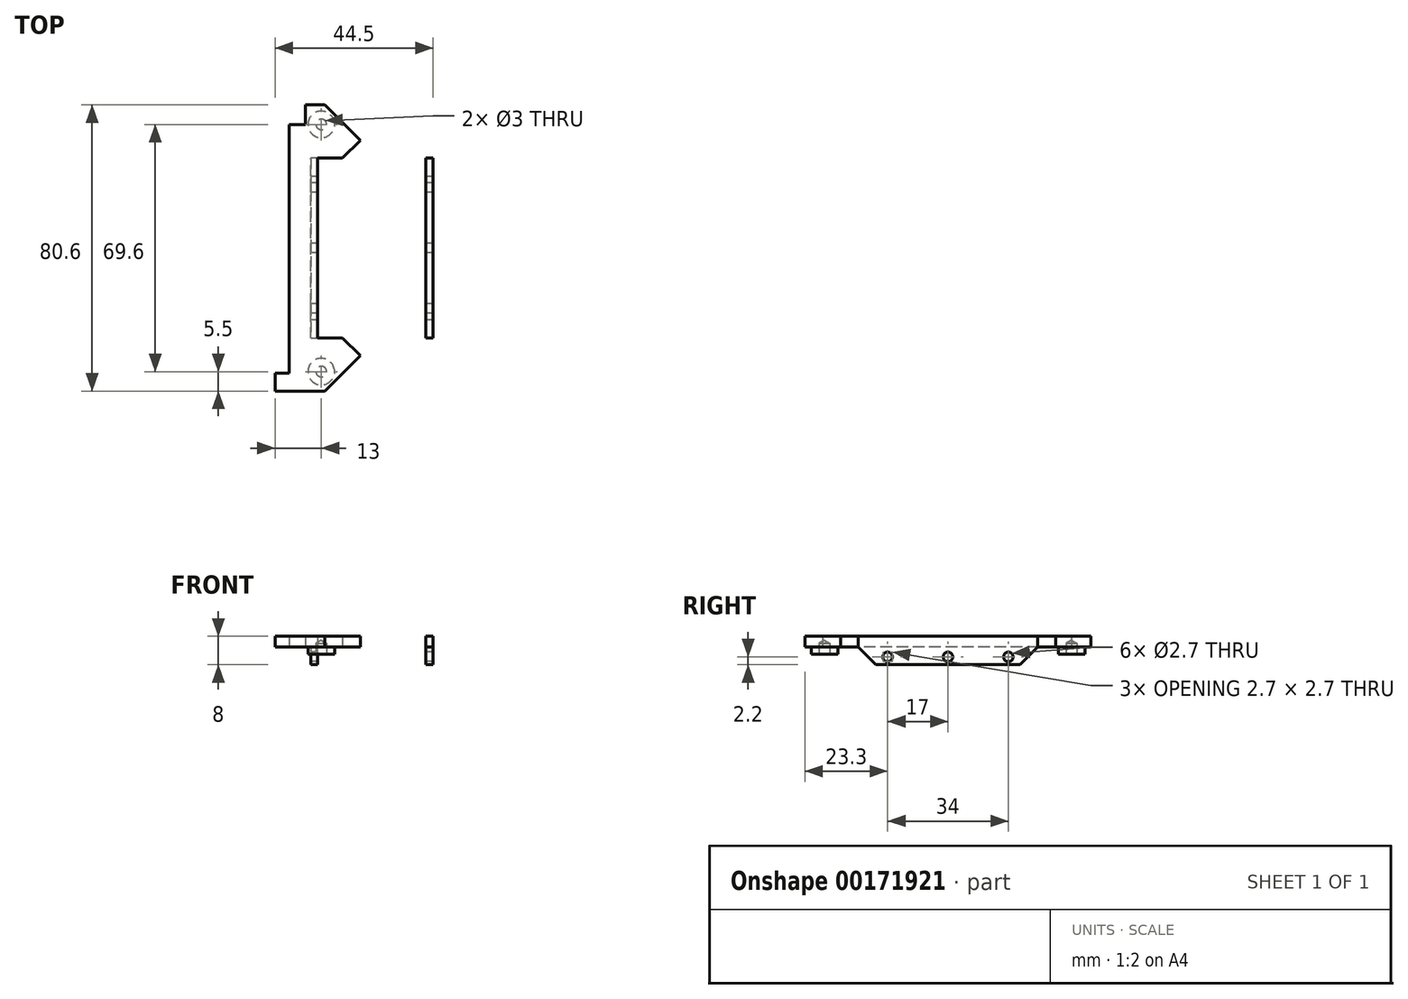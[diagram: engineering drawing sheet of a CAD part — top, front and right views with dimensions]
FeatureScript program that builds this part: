
annotation { "Feature Type Name" : "Feature", "Feature Type Description" : "" }
export const myFeature = defineFeature(function(context is Context, id is Id, definition is map)
    precondition{}
    {
        {
            var Q0;
            Q0=qCreatedBy(makeId("Top.planeOp"),FACE);
            var sketch = newSketch(context, id + "F0", { "sketchPlane" : qUnion([Q0])});
            skLineSegment(sketch, "E0.bottom", {"start": v(18.25, -12.65) * mm, "end": v(-18.25, -12.65) * mm});
            skLineSegment(sketch, "E0.top", {"start": v(18.25, 12.65) * mm, "end": v(-18.25, 12.65) * mm});
            skLineSegment(sketch, "E0.left", {"start": v(18.25, -12.65) * mm, "end": v(18.25, 12.65) * mm});
            skLineSegment(sketch, "E0.right", {"start": v(-18.25, -12.65) * mm, "end": v(-18.25, 12.65) * mm});
            skPoint(sketch, "E0.middle", {"position": v(0, 0) * mm});
            skLineSegment(sketch, "E1.bottom", {"start": v(-15.25, 12.65) * mm, "end": v(15.25, 12.65) * mm});
            skLineSegment(sketch, "E1.top", {"start": v(-15.25, -12.65) * mm, "end": v(15.25, -12.65) * mm});
            skLineSegment(sketch, "E1.left", {"start": v(-15.25, 12.65) * mm, "end": v(-15.25, -12.65) * mm});
            skLineSegment(sketch, "E1.right", {"start": v(15.25, 12.65) * mm, "end": v(15.25, -12.65) * mm});
            skSolve(sketch);
        }
        {
            var Q0;
            {var subQ0=sQuery(id+"F0.wireOp",EDGE,"E0.left");Q0=makeQuery(id+"F0.imprint","IMPRINT",FACE,{"disambiguationData":[TD([[makeQuery(id+"F0.imprint","IMPRINT",EDGE,{"derivedFrom":subQ0}),1.0]])]});}
            var Q1;
            Q1=makeQuery(id+"F0.imprint","IMPRINT",FACE,{"disambiguationData":[TD([[makeQuery(id+"F0.imprint","IMPRINT",EDGE,{"derivedFrom":sQuery(id+"F0.wireOp",EDGE,"E1.bottom")}),-1.0]])]});
            var Q2;
            {var subQ0=sQuery(id+"F0.wireOp",EDGE,"E0.right");Q2=makeQuery(id+"F0.imprint","IMPRINT",FACE,{"disambiguationData":[TD([[makeQuery(id+"F0.imprint","IMPRINT",EDGE,{"derivedFrom":subQ0}),-1.0]])]});}
            extrude(context, id + "F1", {"entities" : qUnion([Q0, Q1, Q2]), "depth" : 3 * mm});
        }
        {
            var Q0;
            {var subQ0=sQuery(id+"F0.wireOp",EDGE,"E0.left");Q0=makeQuery(id+"F0.imprint","IMPRINT",FACE,{"disambiguationData":[TD([[makeQuery(id+"F0.imprint","IMPRINT",EDGE,{"derivedFrom":subQ0}),1.0]])]});}
            var Q1;
            {var subQ0=sQuery(id+"F0.wireOp",EDGE,"E0.right");Q1=makeQuery(id+"F0.imprint","IMPRINT",FACE,{"disambiguationData":[TD([[makeQuery(id+"F0.imprint","IMPRINT",EDGE,{"derivedFrom":subQ0}),-1.0]])]});}
            extrude(context, id + "F2", {"entities" : qUnion([Q0, Q1]), "operationType" : NewBodyOperationType.ADD, "oppositeDirection" : true, "depth" : 5 * mm});
        }
        {
            var Q0;
            Q0=makeQuery(id+"F2.opExtrude","SWEPT_FACE",FACE,{"disambiguationData":[OSD([sQuery(id+"F0.wireOp",EDGE,"E1.right")])]});
            var sketch = newSketch(context, id + "F3", { "sketchPlane" : qUnion([Q0])});
            skLineSegment(sketch, "E2", {"start": v(0, -2.9) * mm, "end": v(0, 13.46) * mm, "construction": true});
            skLineSegment(sketch, "E3", {"start": v(-11.7, -5) * mm, "end": v(7.83, -5) * mm, "construction": true});
            skLineSegment(sketch, "E4", {"start": v(18.8, 0) * mm, "end": v(-9.4, 0) * mm, "construction": true});
            skCircle(sketch, "E5", {"center": v(12.65, -2.8) * mm, "radius": 1.35 * mm});
            skCircle(sketch, "E6", {"center": v(-4.35, -2.8) * mm, "radius": 1.35 * mm});
            skCircle(sketch, "E7.0", {"center": v(-4.35, -2.8) * mm, "radius": 2.35 * mm});
            skCircle(sketch, "E8.0", {"center": v(12.65, -2.8) * mm, "radius": 2.35 * mm});
            skSolve(sketch);
        }
        {
            var Q0;
            {var subQ0=sQuery(id+"F3.wireOp",EDGE,"E5");var subQ1=makeQuery(id+"F2.opExtrude","SWEPT_EDGE",EDGE,{"disambiguationData":[OSD([sQuery(id+"F0.wireOp",EDGE,"E0.bottom"),sQuery(id+"F0.wireOp",EDGE,"E1.top"),sQuery(id+"F0.wireOp",EDGE,"E1.right")])]});var subQ2=makeQuery(id+"F3.imprint","INTERSECT",VERTEX,{"disambiguationData":[OD(0.0)],"derivedFrom":[subQ1,subQ0]});Q0=makeQuery(id+"F3.imprint","IMPRINT",FACE,{"disambiguationData":[TD([[makeQuery(id+"F3.imprint","IMPRINT",EDGE,{"disambiguationData":[TD([[subQ2,1.0]])],"derivedFrom":subQ0}),1.0]])]});}
            var Q1;
            Q1=makeQuery(id+"F3.imprint","IMPRINT",FACE,{"disambiguationData":[TD([[makeQuery(id+"F3.imprint","IMPRINT",EDGE,{"derivedFrom":sQuery(id+"F3.wireOp",EDGE,"E6")}),1.0]])]});
            extrude(context, id + "F4", {"entities" : qUnion([Q0, Q1]), "operationType" : NewBodyOperationType.REMOVE, "endBound" : BoundingType.SYMMETRIC, "oppositeDirection" : true, "depth" : 1000 * mm});
        }
        {
            var Q0;
            Q0=qCreatedBy(makeId("Front.planeOp"),FACE);
            cPlane(context, id + "F5", {"entities" : qUnion([Q0]), "cplaneType" : CPlaneType.OFFSET, "offset" : 12.65 * mm, "width" : 150 * mm, "height" : 150 * mm});
        }
        {
            var Q0;
            Q0=makeQuery(id+"F1.opExtrude","SWEPT_BODY",BODY,{"disambiguationData":[OSD([sQuery(id+"F0.wireOp",EDGE,"E0.left"),sQuery(id+"F0.wireOp",EDGE,"E0.right"),sQuery(id+"F0.wireOp",EDGE,"E1.bottom"),sQuery(id+"F0.wireOp",EDGE,"E1.top")])]});
            var Q1;
            Q1=qCreatedBy(id+"F5.planeOp",FACE);
            mirror(context, id + "F6", {"operationType" : NewBodyOperationType.ADD, "entities" : qUnion([Q0]), "mirrorPlane" : qUnion([Q1])});
        }
        {
            var Q0;
            {var subQ0=sQuery(id+"F0.wireOp",EDGE,"E0.top");Q0=makeQuery(id+"F2.opExtrude","CAP_EDGE",EDGE,{"disambiguationData":[OSD([subQ0]),TDD([makeQuery(id+"F0.imprint","IMPRINT",EDGE,{"disambiguationData":[TD([[makeQuery(id+"F0.imprint","INTERSECT",VERTEX,{"derivedFrom":[subQ0,sQuery(id+"F0.wireOp",EDGE,"E0.right")]}),1.0]])],"derivedFrom":subQ0})])],"isStart":false});}
            var Q1;
            {var subQ0=sQuery(id+"F0.wireOp",EDGE,"E0.top");Q1=makeQuery(id+"F2.opExtrude","CAP_EDGE",EDGE,{"disambiguationData":[OSD([subQ0]),TDD([makeQuery(id+"F0.imprint","IMPRINT",EDGE,{"disambiguationData":[TD([[makeQuery(id+"F0.imprint","INTERSECT",VERTEX,{"derivedFrom":[subQ0,sQuery(id+"F0.wireOp",EDGE,"E0.left")]}),-1.0]])],"derivedFrom":subQ0})])],"isStart":false});}
            var Q2;
            {var subQ0=sQuery(id+"F0.wireOp",EDGE,"E0.top");Q2=makeQuery(id+"F6.opPattern","COPY",EDGE,{"derivedFrom":makeQuery(id+"F2.opExtrude","CAP_EDGE",EDGE,{"disambiguationData":[OSD([subQ0]),TDD([makeQuery(id+"F0.imprint","IMPRINT",EDGE,{"disambiguationData":[TD([[makeQuery(id+"F0.imprint","INTERSECT",VERTEX,{"derivedFrom":[subQ0,sQuery(id+"F0.wireOp",EDGE,"E0.left")]}),-1.0]])],"derivedFrom":subQ0})])],"isStart":false}),"instanceName":"1"});}
            var Q3;
            {var subQ0=sQuery(id+"F0.wireOp",EDGE,"E0.top");Q3=makeQuery(id+"F6.opPattern","COPY",EDGE,{"derivedFrom":makeQuery(id+"F2.opExtrude","CAP_EDGE",EDGE,{"disambiguationData":[OSD([subQ0]),TDD([makeQuery(id+"F0.imprint","IMPRINT",EDGE,{"disambiguationData":[TD([[makeQuery(id+"F0.imprint","INTERSECT",VERTEX,{"derivedFrom":[subQ0,sQuery(id+"F0.wireOp",EDGE,"E0.right")]}),1.0]])],"derivedFrom":subQ0})])],"isStart":false}),"instanceName":"1"});}
            chamfer(context, id + "F7", {"entities" : qUnion([Q0, Q1, Q2, Q3]), "width" : 5 * mm, "tangentPropagation" : true});
        }
        {
            var Q0;
            {var subQ0=sQuery(id+"F0.wireOp",EDGE,"E0.right");var subQ1=makeQuery(id+"F2.boolean.opBoolean","MERGE",FACE,{"derivedFrom":[makeQuery(id+"F1.opExtrude","SWEPT_FACE",FACE,{"disambiguationData":[OSD([subQ0])]}),makeQuery(id+"F2.opExtrude","SWEPT_FACE",FACE,{"disambiguationData":[OSD([subQ0])]})]});Q0=makeQuery(id+"F6.boolean.opBoolean","MERGE",FACE,{"derivedFrom":[subQ1,makeQuery(id+"F6.opPattern","COPY",FACE,{"derivedFrom":subQ1,"instanceName":"1"})]});}
            var sketch = newSketch(context, id + "F8", { "sketchPlane" : qUnion([Q0])});
            skLineSegment(sketch, "E9.bottom", {"start": v(-12.65, 0) * mm, "end": v(37.95, 0) * mm});
            skLineSegment(sketch, "E9.top", {"start": v(-12.65, -6.32) * mm, "end": v(37.95, -6.32) * mm});
            skLineSegment(sketch, "E9.left", {"start": v(-12.65, 0) * mm, "end": v(-12.65, -6.32) * mm});
            skLineSegment(sketch, "E9.right", {"start": v(37.95, 0) * mm, "end": v(37.95, -6.32) * mm});
            skSolve(sketch);
        }
        {
            var Q0;
            Q0=makeQuery(id+"F8.imprint","IMPRINT",FACE,{"disambiguationData":[TD([[makeQuery(id+"F8.imprint","IMPRINT",EDGE,{"derivedFrom":sQuery(id+"F8.wireOp",EDGE,"E9.bottom")}),-1.0]])]});
            extrude(context, id + "F9", {"entities" : qUnion([Q0]), "operationType" : NewBodyOperationType.REMOVE, "oppositeDirection" : true, "depth" : 1 * mm});
        }
        {
            var Q0;
            Q0=qCreatedBy(makeId("Top.planeOp"),FACE);
            var sketch = newSketch(context, id + "F10", { "sketchPlane" : qUnion([Q0])});
            skLineSegment(sketch, "E10.bottom", {"start": v(-18.25, -37.95) * mm, "end": v(-3.25, -37.95) * mm});
            skLineSegment(sketch, "E10.top", {"start": v(-18.25, -52.95) * mm, "end": v(-3.25, -52.95) * mm});
            skLineSegment(sketch, "E10.left", {"start": v(-18.25, -37.95) * mm, "end": v(-18.25, -52.95) * mm});
            skLineSegment(sketch, "E10.right", {"start": v(-3.25, -37.95) * mm, "end": v(-3.25, -52.95) * mm});
            skLineSegment(sketch, "E11.bottom", {"start": v(-18.25, 12.65) * mm, "end": v(-3.25, 12.65) * mm});
            skLineSegment(sketch, "E11.top", {"start": v(-18.25, 27.65) * mm, "end": v(-3.25, 27.65) * mm});
            skLineSegment(sketch, "E11.left", {"start": v(-18.25, 12.65) * mm, "end": v(-18.25, 27.65) * mm});
            skLineSegment(sketch, "E11.right", {"start": v(-3.25, 12.65) * mm, "end": v(-3.25, 27.65) * mm});
            skSolve(sketch);
        }
        {
            var Q0;
            Q0 = qSketchRegion(id + "F10", true);
            extrude(context, id + "F11", {"entities" : qUnion([Q0]), "operationType" : NewBodyOperationType.ADD, "depth" : 3 * mm});
        }
        {
            var Q0;
            {var subQ0=makeQuery(id+"F1.opExtrude","CAP_FACE",FACE,{"disambiguationData":[OSD([sQuery(id+"F0.wireOp",EDGE,"E0.bottom"),sQuery(id+"F0.wireOp",EDGE,"E0.top"),sQuery(id+"F0.wireOp",EDGE,"E0.left"),sQuery(id+"F0.wireOp",EDGE,"E0.right"),sQuery(id+"F0.wireOp",EDGE,"E1.bottom"),sQuery(id+"F0.wireOp",EDGE,"E1.top")])],"isStart":true});Q0=makeQuery(id+"F11.boolean.opBoolean","MERGE",FACE,{"derivedFrom":[makeQuery(id+"F6.boolean.opBoolean","MERGE",FACE,{"derivedFrom":[subQ0,makeQuery(id+"F6.opPattern","COPY",FACE,{"derivedFrom":subQ0,"instanceName":"1"})]}),makeQuery(id+"F9.boolean.opBoolean","COPY",FACE,{"derivedFrom":makeQuery(id+"F9.opExtrude","SWEPT_FACE",FACE,{"disambiguationData":[OSD([sQuery(id+"F8.wireOp",EDGE,"E9.bottom")])]})}),makeQuery(id+"F11.opExtrude","CAP_FACE",FACE,{"disambiguationData":[OSD([sQuery(id+"F10.wireOp",EDGE,"pW5Quktj-L34n-hhZY-v1Ix-rfs9Iihu1468.bottom"),sQuery(id+"F10.wireOp",EDGE,"pW5Quktj-L34n-hhZY-v1Ix-rfs9Iihu1468.top"),sQuery(id+"F10.wireOp",EDGE,"pW5Quktj-L34n-hhZY-v1Ix-rfs9Iihu1468.left"),sQuery(id+"F10.wireOp",EDGE,"pW5Quktj-L34n-hhZY-v1Ix-rfs9Iihu1468.right")])],"isStart":true}),makeQuery(id+"F11.opExtrude","CAP_FACE",FACE,{"disambiguationData":[OSD([sQuery(id+"F10.wireOp",EDGE,"H2ijIvu5-2ODO-Xeke-0aQG-66x5qS3q1Ywc.bottom"),sQuery(id+"F10.wireOp",EDGE,"H2ijIvu5-2ODO-Xeke-0aQG-66x5qS3q1Ywc.top"),sQuery(id+"F10.wireOp",EDGE,"H2ijIvu5-2ODO-Xeke-0aQG-66x5qS3q1Ywc.left"),sQuery(id+"F10.wireOp",EDGE,"H2ijIvu5-2ODO-Xeke-0aQG-66x5qS3q1Ywc.right")])],"isStart":true})]});}
            var sketch = newSketch(context, id + "F12", { "sketchPlane" : qUnion([Q0])});
            skLineSegment(sketch, "E12.bottom", {"start": v(-18.25, 52.95) * mm, "end": v(-22.25, 52.95) * mm});
            skLineSegment(sketch, "E12.top", {"start": v(-18.25, 47.95) * mm, "end": v(-22.25, 47.95) * mm});
            skLineSegment(sketch, "E12.left", {"start": v(-18.25, 52.95) * mm, "end": v(-18.25, 47.95) * mm});
            skLineSegment(sketch, "E12.right", {"start": v(-22.25, 52.95) * mm, "end": v(-22.25, 47.95) * mm});
            skLineSegment(sketch, "E13.bottom", {"start": v(-18.25, -27.65) * mm, "end": v(-13.75, -27.65) * mm});
            skLineSegment(sketch, "E13.top", {"start": v(-18.25, -22.15) * mm, "end": v(-13.75, -22.15) * mm});
            skLineSegment(sketch, "E13.left", {"start": v(-18.25, -27.65) * mm, "end": v(-18.25, -22.15) * mm});
            skLineSegment(sketch, "E13.right", {"start": v(-13.75, -27.65) * mm, "end": v(-13.75, -22.15) * mm});
            skSolve(sketch);
        }
        {
            var Q0;
            Q0=makeQuery(id+"F12.imprint","IMPRINT",FACE,{"disambiguationData":[TD([[makeQuery(id+"F12.imprint","IMPRINT",EDGE,{"derivedFrom":sQuery(id+"F12.wireOp",EDGE,"E12.bottom")}),1.0]])]});
            extrude(context, id + "F13", {"entities" : qUnion([Q0]), "operationType" : NewBodyOperationType.ADD, "oppositeDirection" : true, "depth" : 3 * mm});
        }
        {
            var Q0;
            Q0=makeQuery(id+"F12.imprint","IMPRINT",FACE,{"disambiguationData":[TD([[makeQuery(id+"F12.imprint","IMPRINT",EDGE,{"derivedFrom":sQuery(id+"F12.wireOp",EDGE,"E13.bottom")}),1.0]])]});
            extrude(context, id + "F14", {"entities" : qUnion([Q0]), "operationType" : NewBodyOperationType.REMOVE, "oppositeDirection" : true, "depth" : 25 * mm});
        }
        {
            var Q0;
            {var subQ0=sQuery(id+"F0.wireOp",EDGE,"E0.right");var subQ1=makeQuery(id+"F2.boolean.opBoolean","MERGE",FACE,{"derivedFrom":[makeQuery(id+"F1.opExtrude","SWEPT_FACE",FACE,{"disambiguationData":[OSD([subQ0])]}),makeQuery(id+"F2.opExtrude","SWEPT_FACE",FACE,{"disambiguationData":[OSD([subQ0])]})]});Q0=makeQuery(id+"F11.boolean.opBoolean","MERGE",FACE,{"derivedFrom":[makeQuery(id+"F6.boolean.opBoolean","MERGE",FACE,{"derivedFrom":[subQ1,makeQuery(id+"F6.opPattern","COPY",FACE,{"derivedFrom":subQ1,"instanceName":"1"})]}),makeQuery(id+"F11.opExtrude","SWEPT_FACE",FACE,{"disambiguationData":[OSD([sQuery(id+"F10.wireOp",EDGE,"E10.left")])]}),makeQuery(id+"F11.opExtrude","SWEPT_FACE",FACE,{"disambiguationData":[OSD([sQuery(id+"F10.wireOp",EDGE,"E11.left")])]})]});}
            var Q1;
            Q1=makeQuery(id+"F13.opExtrude","SWEPT_FACE",FACE,{"disambiguationData":[OSD([sQuery(id+"F12.wireOp",EDGE,"E12.right")])]});
            var Q2;
            Q2=makeQuery(id+"F14.boolean.opBoolean","COPY",FACE,{"derivedFrom":makeQuery(id+"F14.opExtrude","SWEPT_FACE",FACE,{"disambiguationData":[OSD([sQuery(id+"F12.wireOp",EDGE,"E13.right")])]})});
            extrude(context, id + "F15", {"entities" : qUnion([Q0, Q1, Q2]), "operationType" : NewBodyOperationType.ADD, "depth" : 5 * mm});
        }
        {
            var Q0;
            {var subQ0=sQuery(id+"F10.wireOp",EDGE,"E11.left");var subQ1=sQuery(id+"F10.wireOp",EDGE,"E10.left");var subQ2=sQuery(id+"F8.wireOp",EDGE,"E9.bottom");var subQ3=sQuery(id+"F12.wireOp",EDGE,"E12.right");var subQ4=makeQuery(id+"F1.opExtrude","CAP_FACE",FACE,{"disambiguationData":[OSD([sQuery(id+"F0.wireOp",EDGE,"E0.bottom"),sQuery(id+"F0.wireOp",EDGE,"E0.top"),sQuery(id+"F0.wireOp",EDGE,"E0.left"),sQuery(id+"F0.wireOp",EDGE,"E0.right"),sQuery(id+"F0.wireOp",EDGE,"E1.bottom"),sQuery(id+"F0.wireOp",EDGE,"E1.top")])],"isStart":true});Q0=makeQuery(id+"F15.boolean.opBoolean","MERGE",FACE,{"derivedFrom":[makeQuery(id+"F13.boolean.opBoolean","MERGE",FACE,{"derivedFrom":[makeQuery(id+"F11.boolean.opBoolean","MERGE",FACE,{"derivedFrom":[makeQuery(id+"F6.boolean.opBoolean","MERGE",FACE,{"derivedFrom":[subQ4,makeQuery(id+"F6.opPattern","COPY",FACE,{"derivedFrom":subQ4,"instanceName":"1"})]}),makeQuery(id+"F9.boolean.opBoolean","COPY",FACE,{"derivedFrom":makeQuery(id+"F9.opExtrude","SWEPT_FACE",FACE,{"disambiguationData":[OSD([subQ2])]})}),makeQuery(id+"F11.opExtrude","CAP_FACE",FACE,{"disambiguationData":[OSD([sQuery(id+"F10.wireOp",EDGE,"E10.bottom"),sQuery(id+"F10.wireOp",EDGE,"E10.top"),subQ1,sQuery(id+"F10.wireOp",EDGE,"E10.right")])],"isStart":true}),makeQuery(id+"F11.opExtrude","CAP_FACE",FACE,{"disambiguationData":[OSD([sQuery(id+"F10.wireOp",EDGE,"E11.bottom"),sQuery(id+"F10.wireOp",EDGE,"E11.top"),subQ0,sQuery(id+"F10.wireOp",EDGE,"E11.right")])],"isStart":true})]}),makeQuery(id+"F13.opExtrude","CAP_FACE",FACE,{"disambiguationData":[OSD([sQuery(id+"F12.wireOp",EDGE,"E12.bottom"),sQuery(id+"F12.wireOp",EDGE,"E12.top"),sQuery(id+"F12.wireOp",EDGE,"E12.left"),subQ3])],"isStart":true})]}),makeQuery(id+"F15.opExtrude","SWEPT_FACE",FACE,{"disambiguationData":[OSD([subQ3]),TDD([makeQuery(id+"F13.opExtrude","CAP_EDGE",EDGE,{"disambiguationData":[OSD([subQ3])],"isStart":true})])]}),makeQuery(id+"F15.opExtrude","SWEPT_FACE",FACE,{"disambiguationData":[OSD([sQuery(id+"F12.wireOp",EDGE,"E13.right")])]}),makeQuery(id+"F15.opExtrude","SWEPT_FACE",FACE,{"disambiguationData":[OSD([subQ2,subQ1,subQ0])]})]});}
            var sketch = newSketch(context, id + "F16", { "sketchPlane" : qUnion([Q0])});
            skCircle(sketch, "E14", {"center": v(-14.25, 47.45) * mm, "radius": 3.75 * mm});
            skCircle(sketch, "E15", {"center": v(-14.25, -22.15) * mm, "radius": 3.75 * mm});
            skSolve(sketch);
        }
        {
            var Q0;
            Q0=makeQuery(id+"F16.imprint","IMPRINT",FACE,{"disambiguationData":[TD([[makeQuery(id+"F16.imprint","IMPRINT",EDGE,{"derivedFrom":sQuery(id+"F16.wireOp",EDGE,"E15")}),1.0]])]});
            var Q1;
            Q1=makeQuery(id+"F16.imprint","IMPRINT",FACE,{"disambiguationData":[TD([[makeQuery(id+"F16.imprint","IMPRINT",EDGE,{"derivedFrom":sQuery(id+"F16.wireOp",EDGE,"E14")}),1.0]])]});
            extrude(context, id + "F17", {"entities" : qUnion([Q0, Q1]), "operationType" : NewBodyOperationType.ADD, "depth" : 2 * mm});
        }
        {
            var Q0;
            Q0=makeQuery(id+"F17.opExtrude","CAP_FACE",FACE,{"disambiguationData":[OSD([sQuery(id+"F16.wireOp",EDGE,"E14")])],"isStart":false});
            var sketch = newSketch(context, id + "F18", { "sketchPlane" : qUnion([Q0])});
            skCircle(sketch, "E16", {"center": v(-14.25, 47.45) * mm, "radius": 1 * mm});
            skSolve(sketch);
        }
        {
            var Q0;
            Q0=makeQuery(id+"F17.opExtrude","CAP_FACE",FACE,{"disambiguationData":[OSD([sQuery(id+"F16.wireOp",EDGE,"E15")])],"isStart":false});
            var sketch = newSketch(context, id + "F19", { "sketchPlane" : qUnion([Q0])});
            skCircle(sketch, "E17", {"center": v(-14.25, -22.15) * mm, "radius": 1 * mm});
            skSolve(sketch);
        }
        {
            var Q0;
            Q0=sQuery(id+"F18.wireOp",VERTEX,"E16.center");
            var Q1;
            Q1=sQuery(id+"F19.wireOp",VERTEX,"E17.center");
            var Q2;
            Q2=makeQuery(id+"F1.opExtrude","SWEPT_BODY",BODY,{"disambiguationData":[OSD([sQuery(id+"F0.wireOp",EDGE,"E0.bottom"),sQuery(id+"F0.wireOp",EDGE,"E0.top"),sQuery(id+"F0.wireOp",EDGE,"E0.left"),sQuery(id+"F0.wireOp",EDGE,"E0.right"),sQuery(id+"F0.wireOp",EDGE,"E1.bottom"),sQuery(id+"F0.wireOp",EDGE,"E1.top")])]});
            hole(context, id + "F20", {"style" : HoleStyle.C_BORE, "endStyle" : HoleEndStyle.BLIND, "holeDiameter" : 3 * mm, "cBoreDiameter" : 3 * mm, "cBoreDepth" : 3 * mm, "holeDepth" : 3 * mm, "tappedDepth" : 12 * mm, "tapClearance" : 3, "locations" : qUnion([Q0, Q1]), "scope" : qUnion([Q2])});
        }
        {
            var Q0;
            Q0=makeQuery(id+"F11.opExtrude","SWEPT_EDGE",EDGE,{"disambiguationData":[OSD([sQuery(id+"F10.wireOp",EDGE,"E11.top"),sQuery(id+"F10.wireOp",EDGE,"E11.right")])]});
            var Q1;
            Q1=makeQuery(id+"F11.opExtrude","SWEPT_EDGE",EDGE,{"disambiguationData":[OSD([sQuery(id+"F10.wireOp",EDGE,"E10.top"),sQuery(id+"F10.wireOp",EDGE,"E10.right")])]});
            chamfer(context, id + "F21", {"entities" : qUnion([Q0, Q1]), "width" : 10 * mm, "tangentPropagation" : true});
        }
        {
            var Q0;
            {var subQ0=sQuery(id+"F0.wireOp",EDGE,"E0.left");var subQ1=makeQuery(id+"F2.boolean.opBoolean","MERGE",FACE,{"derivedFrom":[makeQuery(id+"F1.opExtrude","SWEPT_FACE",FACE,{"disambiguationData":[OSD([subQ0])]}),makeQuery(id+"F2.opExtrude","SWEPT_FACE",FACE,{"disambiguationData":[OSD([subQ0])]})]});Q0=makeQuery(id+"F6.boolean.opBoolean","MERGE",FACE,{"derivedFrom":[subQ1,makeQuery(id+"F6.opPattern","COPY",FACE,{"derivedFrom":subQ1,"instanceName":"1"})]});}
            extrude(context, id + "F22", {"entities" : qUnion([Q0]), "operationType" : NewBodyOperationType.REMOVE, "oppositeDirection" : true, "depth" : 1 * mm});
        }
        {
            var Q0;
            Q0=makeQuery(id+"F11.opExtrude","SWEPT_EDGE",EDGE,{"disambiguationData":[OSD([sQuery(id+"F10.wireOp",EDGE,"E10.bottom"),sQuery(id+"F10.wireOp",EDGE,"E10.right")])]});
            var Q1;
            Q1=makeQuery(id+"F11.opExtrude","SWEPT_EDGE",EDGE,{"disambiguationData":[OSD([sQuery(id+"F10.wireOp",EDGE,"E11.bottom"),sQuery(id+"F10.wireOp",EDGE,"E11.right")])]});
            chamfer(context, id + "F23", {"entities" : qUnion([Q0, Q1]), "width" : 5 * mm, "tangentPropagation" : true});
        }
    });
